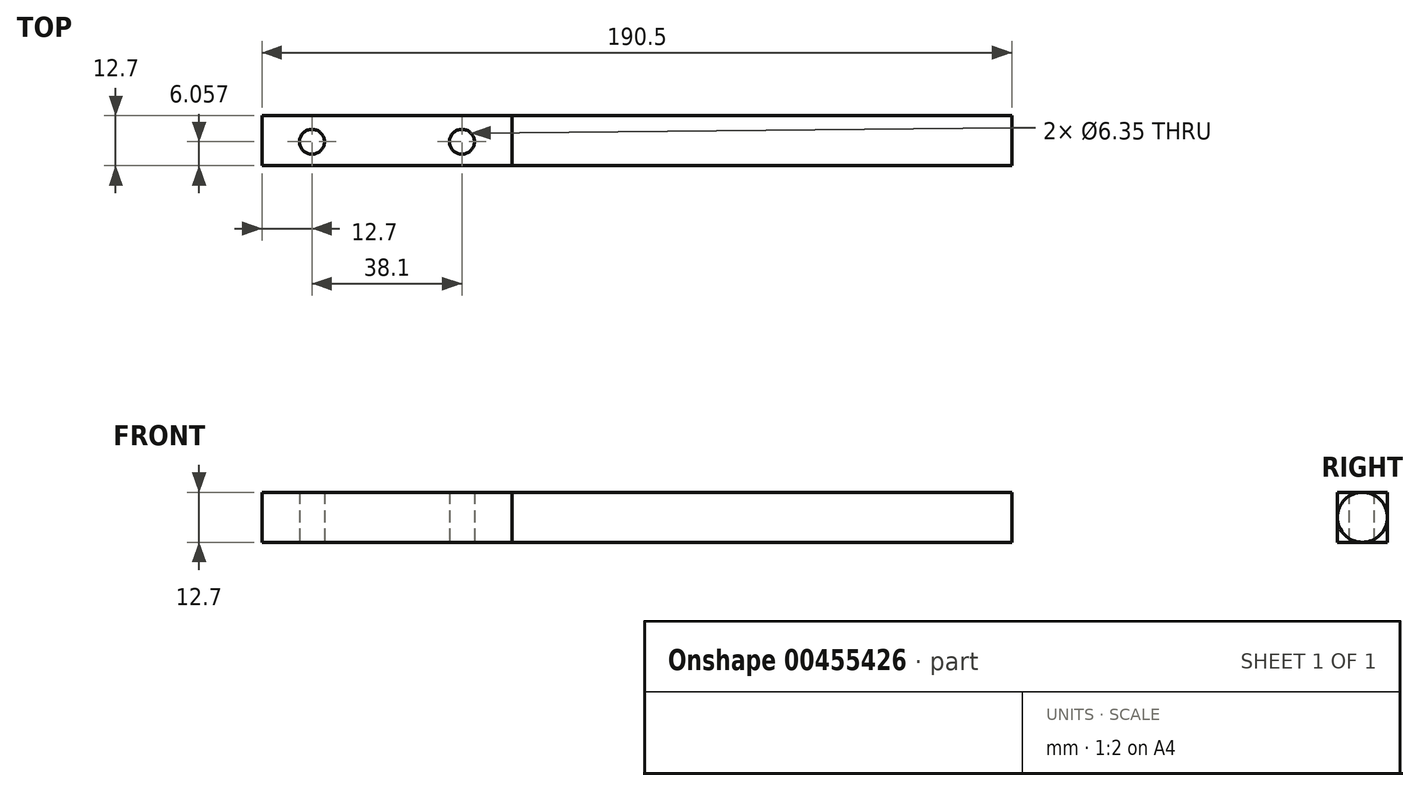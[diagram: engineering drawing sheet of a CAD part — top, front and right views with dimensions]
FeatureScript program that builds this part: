
annotation { "Feature Type Name" : "Feature", "Feature Type Description" : "" }
export const myFeature = defineFeature(function(context is Context, id is Id, definition is map)
    precondition{}
    {
        {
            var Q0;
            Q0=qCreatedBy(makeId("Top.planeOp"),FACE);
            var sketch = newSketch(context, id + "F0", { "sketchPlane" : qUnion([Q0])});
            skLineSegment(sketch, "E0.bottom", {"start": v(-37.99, -14.19) * mm, "end": v(25.51, -14.19) * mm});
            skLineSegment(sketch, "E0.top", {"start": v(-37.99, -26.89) * mm, "end": v(25.51, -26.89) * mm});
            skLineSegment(sketch, "E0.left", {"start": v(-37.99, -14.19) * mm, "end": v(-37.99, -26.89) * mm});
            skLineSegment(sketch, "E0.right", {"start": v(25.51, -14.19) * mm, "end": v(25.51, -26.89) * mm});
            skCircle(sketch, "E1", {"center": v(-25.29, -20.83) * mm, "radius": 3.18 * mm});
            skCircle(sketch, "E2", {"center": v(12.81, -20.83) * mm, "radius": 3.18 * mm});
            skSolve(sketch);
        }
        {
            var Q0;
            Q0=makeQuery(id+"F0.imprint","IMPRINT",FACE,{"disambiguationData":[TD([[makeQuery(id+"F0.imprint","IMPRINT",EDGE,{"derivedFrom":sQuery(id+"F0.wireOp",EDGE,"E0.bottom")}),-1.0]])]});
            extrude(context, id + "F1", {"entities" : qUnion([Q0]), "depth" : 12.7 * mm});
        }
        {
            var Q0;
            Q0=makeQuery(id+"F1.opExtrude","SWEPT_FACE",FACE,{"disambiguationData":[OSD([sQuery(id+"F0.wireOp",EDGE,"E0.right")])]});
            var sketch = newSketch(context, id + "F2", { "sketchPlane" : qUnion([Q0])});
            skCircle(sketch, "E3", {"center": v(-20.54, 6.35) * mm, "radius": 6.35 * mm});
            skPoint(sketch, "E3.centerSnap0", {"position": v(-20.54, 0) * mm});
            skSolve(sketch);
        }
        {
            var Q0;
            {var subQ0=sQuery(id+"F2.wireOp",EDGE,"E3");var subQ1=sQuery(id+"F0.wireOp",EDGE,"E0.right");var subQ2=makeQuery(id+"F2.imprint","INTERSECT",VERTEX,{"derivedFrom":[makeQuery(id+"F1.opExtrude","CAP_EDGE",EDGE,{"disambiguationData":[OSD([subQ1])],"isStart":false}),subQ0]});Q0=makeQuery(id+"F2.imprint","IMPRINT",FACE,{"disambiguationData":[TD([[makeQuery(id+"F2.imprint","IMPRINT",EDGE,{"disambiguationData":[TD([[subQ2,1.0]])],"derivedFrom":subQ0}),1.0]])]});}
            extrude(context, id + "F3", {"entities" : qUnion([Q0]), "operationType" : NewBodyOperationType.ADD, "depth" : 127 * mm});
        }
    });
